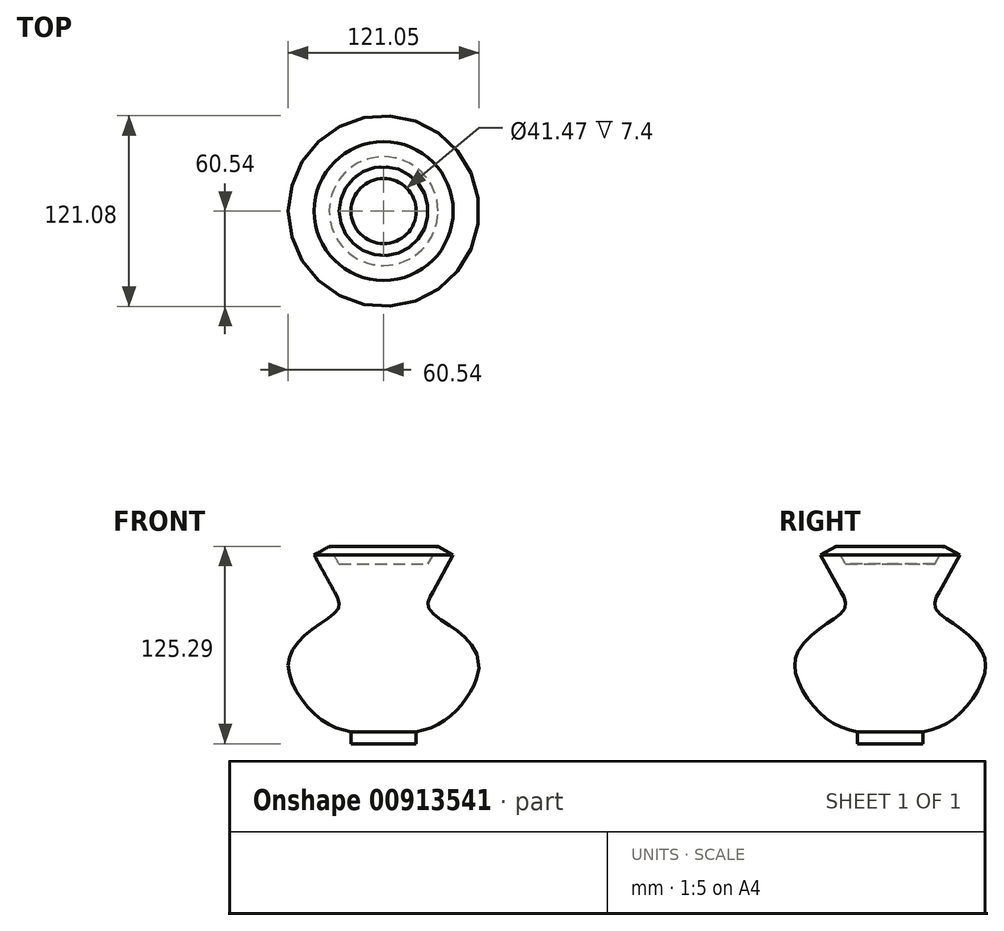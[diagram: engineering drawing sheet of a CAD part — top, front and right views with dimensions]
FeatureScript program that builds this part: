
annotation { "Feature Type Name" : "Feature", "Feature Type Description" : "" }
export const myFeature = defineFeature(function(context is Context, id is Id, definition is map)
    precondition{}
    {
        {
            var Q0;
            Q0=qCreatedBy(makeId("Front.planeOp"),FACE);
            var sketch = newSketch(context, id + "F0", { "sketchPlane" : qUnion([Q0])});
            skLineSegment(sketch, "E0", {"start": v(0, 49.56) * mm, "end": v(28.33, 49.56) * mm});
            skLineSegment(sketch, "E1", {"start": v(28.33, 49.56) * mm, "end": v(34.52, 60.77) * mm});
            skLineSegment(sketch, "E2", {"start": v(34.52, 60.77) * mm, "end": v(44.17, 55.45) * mm});
            skLineSegment(sketch, "E3", {"start": v(44.17, 55.45) * mm, "end": v(31.22, 31.99) * mm});
            skFitSpline(sketch, "E4", {"points": [v(31.22, 31.99) * mm, v(28.44, 22.12) * mm, v(42.63, 10.1) * mm, v(59.58, -8.71) * mm, v(56.2, -29.68) * mm, v(38, -50.33) * mm, v(20.73, -57.12) * mm], "startDerivative": vector(-47.03, -85.22) * mm, "endDerivative": vector(-107.36, -28.02) * mm});
            skLineSegment(sketch, "E5", {"start": v(20.73, -57.12) * mm, "end": v(20.73, -64.52) * mm});
            skLineSegment(sketch, "E6", {"start": v(20.73, -64.52) * mm, "end": v(0, -64.52) * mm});
            skLineSegment(sketch, "E7", {"start": v(0, 56.7) * mm, "end": v(0, -70.74) * mm});
            skPoint(sketch, "E8.end.orphan", {"position": v(-56.06, 49.56) * mm});
            skLineSegment(sketch, "E9.MirrorCS", {"start": v(0, 49.56) * mm, "end": v(-28.33, 49.56) * mm});
            skLineSegment(sketch, "E10.MirrorCS", {"start": v(-28.33, 49.56) * mm, "end": v(-34.52, 60.77) * mm});
            skLineSegment(sketch, "E11.MirrorCS", {"start": v(-34.52, 60.77) * mm, "end": v(-44.17, 55.45) * mm});
            skLineSegment(sketch, "E12.MirrorCS", {"start": v(-44.17, 55.45) * mm, "end": v(-31.22, 31.99) * mm});
            skFitSpline(sketch, "E13.MirrorCS", {"points": [v(-31.22, 31.99) * mm, v(-28.44, 22.12) * mm, v(-42.63, 10.1) * mm, v(-59.58, -8.71) * mm, v(-56.2, -29.68) * mm, v(-38, -50.33) * mm, v(-20.73, -57.12) * mm], "startDerivative": vector(47.03, -85.22) * mm, "endDerivative": vector(107.36, -28.02) * mm});
            skLineSegment(sketch, "E14.MirrorCS", {"start": v(-20.73, -57.12) * mm, "end": v(-20.73, -64.52) * mm});
            skLineSegment(sketch, "E15.MirrorCS", {"start": v(-20.73, -64.52) * mm, "end": v(0, -64.52) * mm});
            skSolve(sketch);
        }
        {
            var Q0;
            Q0=sQuery(id+"F0.wireOp",EDGE,"E0");
            var Q1;
            Q1=sQuery(id+"F0.wireOp",EDGE,"E1");
            var Q2;
            Q2=sQuery(id+"F0.wireOp",EDGE,"E2");
            var Q3;
            Q3=sQuery(id+"F0.wireOp",EDGE,"E3");
            var Q4;
            Q4=sQuery(id+"F0.wireOp",EDGE,"E4");
            var Q5;
            Q5=sQuery(id+"F0.wireOp",EDGE,"E5");
            var Q6;
            Q6=sQuery(id+"F0.wireOp",EDGE,"E6");
            var Q7;
            Q7=sQuery(id+"F0.wireOp",EDGE,"E7");
            revolve(context, id + "F1", {"bodyType" : ToolBodyType.SURFACE, "surfaceOperationType" : NewSurfaceOperationType.NEW, "surfaceEntities" : qUnion([Q0, Q1, Q2, Q3, Q4, Q5, Q6]), "axis" : qUnion([Q7]), "revolveType" : RevolveType.FULL});
        }
    });
